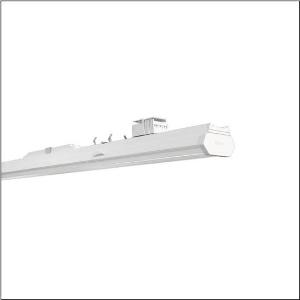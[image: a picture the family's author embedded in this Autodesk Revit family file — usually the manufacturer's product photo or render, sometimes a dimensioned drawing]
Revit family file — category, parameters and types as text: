
# Revit family: licross_r__11_protected_extreme_mo_51tp12dn49xge_ea06
name_source: partatom
category: Lighting Fixtures
units: mm (PartAtom-declared; Revit-internal decimal feet)

## family parameters
Cut with Voids When Loaded = No
Host = Face
Light Source = No
Part Type = Normal
Room Calculation Point = No
Round Connector Dimension = Use Diameter
Shared = No

## types (1)
- --- (1 x LED, 9020 lm, 51 W, 4000K)
    Apparent Load = 51 VA
    CIE Flux Codes = 73 92 98 99 100
    Color Rendering = 80
    Color Temperature = 4000K
    Default Elevation = 1800 mm
    Description = Licross® 11 Protected extreme MO, luminaire insert, of sheet steel, galvanised, coil coated, white, length: 1.500mm, width: 90mm, height: 101mm, LED rated luminous flux: 9.020lm, light colour: 840, SDCM (Standard Deviation of Colour Matching)MacAdam ≤ 2 SDCM (initial), control gear: DALI 2, with plug, 5-pole, with phase selection, mains connection: 220..240V, AC, 50/60Hz, rated input power: 51W, internal wiring halogen-free, primary optical cover: cover, of PMMA, light emission: direct distribution, primary light characteristic: symmetric, protection rating (complete): IP64, insulation class (complete): insulation class I (protective earthing), certification: CE, ENEC, VDE, UKCA, protection symbol: D if used in an environment with conductive dust loads with corresponding accessories, impact resistance: IK06, permissible ambient temperature for indoor applications: -40..+50°C, LABS conformity tested according to VDMA 24364:2018-05, reducing of maximum allowable ambient temperature of 5°C with ceiling mounting, corresponds to IFS (International Featured Standards) requirements for safety and quality in the food industry, packaging unit: 1 piece
    Height = 92 mm
    Lamp = 1 x LED
    Lamp Light Flux = 9020 lm
    Lamp Power = 51 W
    Lamp count = 1
    Length = 1500 mm
    Luminous efficacy = 177 lm/W
    Manufacturer = Siteco
    ModVariant = No
    Model = 51TP12DN49XGE
    Mounting Place = Ceiling
    Mounting Type = Pendant
    Number of Poles = 1
    OnlyDefault = Yes
    Power Factor = 1
    Product Name = Licross® 11 Protected extreme MO
    Product group = luminaire insert | ceiling pendant
    ProductGroupID = 901
    Protection Class = Protection class I
    Protection Degree = IP 64
    RLX_Detail_Level = 1
    RLX_Emergency_Light_Flux = 0 lm
    RLX_Emergency_Type = 0
    RLX_Emergency_Type_DB = No
    RlxData = <blob elided: 24629 chars, md5=3184dd69>
    Socket = socket
    Standby Power = 0 W
    System Light Flux = 9020 lm
    System Power = 51 W
    Type Comments = factory setting: luminous flux: 100 % | dim-lin: 254 | 339 mA
    Type Image = l_1256148.jpg
    URL = http://relux.com
    VarID = @adj_019083
    Voltage = 0 V
    Weight = 0.00 kg
    Width = 88 mm

## geometry (parser evidence)
native form markers: Blend x4, Sweep x10
no freeform markers — native parametric forms only
